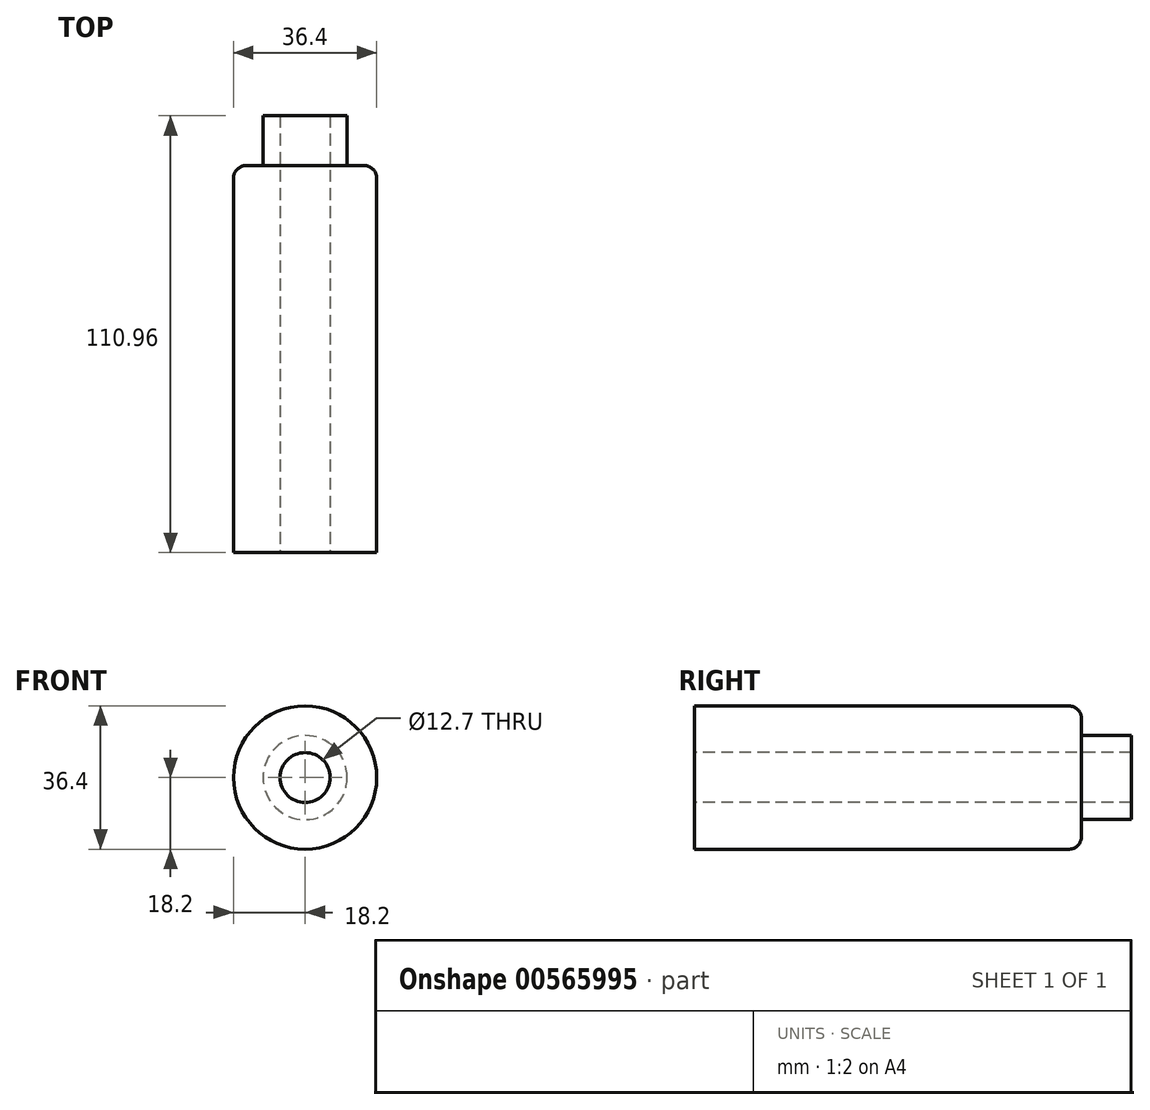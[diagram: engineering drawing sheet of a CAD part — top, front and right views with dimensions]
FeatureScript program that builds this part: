
annotation { "Feature Type Name" : "Feature", "Feature Type Description" : "" }
export const myFeature = defineFeature(function(context is Context, id is Id, definition is map)
    precondition{}
    {
        {
            var Q0;
            Q0=qCreatedBy(makeId("Front.planeOp"),FACE);
            var sketch = newSketch(context, id + "F0", { "sketchPlane" : qUnion([Q0])});
            skCircle(sketch, "E0", {"center": v(0, 0) * mm, "radius": 18.2 * mm});
            skSolve(sketch);
        }
        {
            var Q0;
            Q0=makeQuery(id+"F0.imprint","IMPRINT",FACE,{"disambiguationData":[TD([[makeQuery(id+"F0.imprint","IMPRINT",EDGE,{"derivedFrom":sQuery(id+"F0.wireOp",EDGE,"E0")}),1.0]])]});
            var Q1;
            Q1=sQuery(id+"F0.wireOp",EDGE,"E0");
            extrude(context, id + "F1", {"entities" : qUnion([Q0]), "surfaceEntities" : qUnion([Q1]), "oppositeDirection" : true, "depth" : 98.3 * mm, "offsetDistance" : 25.4 * mm});
        }
        {
            var Q0;
            Q0=makeQuery(id+"F1.opExtrude","CAP_EDGE",EDGE,{"disambiguationData":[OSD([sQuery(id+"F0.wireOp",EDGE,"E0")])],"isStart":false});
            fillet(context, id + "F2", {"entities" : qUnion([Q0]), "radius" : 3.22 * mm, "tangentPropagation" : true, "allowEdgeOverflow" : false});
        }
        {
            var Q0;
            Q0=makeQuery(id+"F1.opExtrude","CAP_FACE",FACE,{"disambiguationData":[OSD([sQuery(id+"F0.wireOp",EDGE,"E0")])],"isStart":true});
            var sketch = newSketch(context, id + "F3", { "sketchPlane" : qUnion([Q0])});
            skCircle(sketch, "E1", {"center": v(0, 0) * mm, "radius": 10.67 * mm});
            skSolve(sketch);
        }
        {
            var Q0;
            Q0 = qSketchRegion(id + "F3", true);
            extrude(context, id + "F4", {"entities" : qUnion([Q0]), "operationType" : NewBodyOperationType.ADD, "endBound" : BoundingType.THROUGH_ALL, "oppositeDirection" : true, "depth" : 78.28 * mm, "offsetDistance" : 25.4 * mm});
        }
        {
            var Q0;
            Q0=makeQuery(id+"F1.opExtrude","CAP_FACE",FACE,{"disambiguationData":[OSD([sQuery(id+"F0.wireOp",EDGE,"E0")])],"isStart":true});
            var sketch = newSketch(context, id + "F5", { "sketchPlane" : qUnion([Q0])});
            skCircle(sketch, "E2", {"center": v(0, 0) * mm, "radius": 12.6 * mm});
            skSolve(sketch);
        }
        {
            var Q0;
            Q0=sQuery(id+"F5.wireOp",VERTEX,"E2.center");
            var Q1;
            Q1=makeQuery(id+"F1.opExtrude","SWEPT_BODY",BODY,{"disambiguationData":[OSD([sQuery(id+"F0.wireOp",EDGE,"E0")])]});
            hole(context, id + "F6", {"style" : HoleStyle.SIMPLE, "endStyle" : HoleEndStyle.THROUGH, "holeDiameter" : 12.7 * mm, "isTappedThrough" : true, "tappedDepth" : 12.7 * mm, "tapClearance" : 3, "locations" : qUnion([Q0]), "scope" : qUnion([Q1])});
        }
    });
